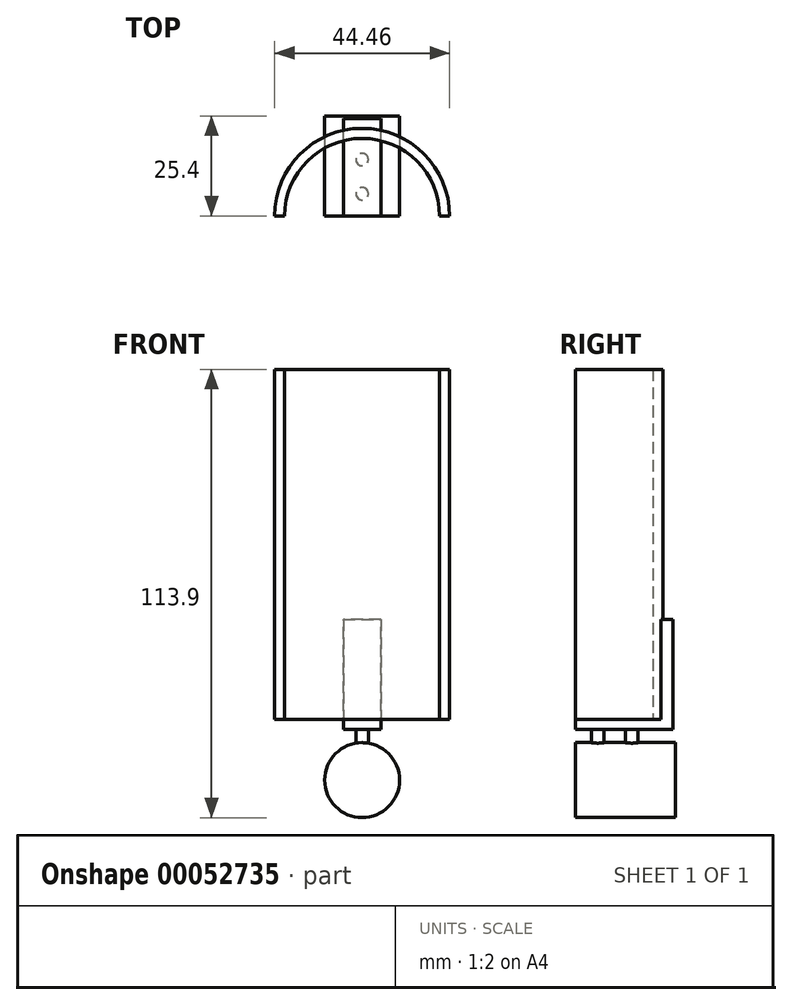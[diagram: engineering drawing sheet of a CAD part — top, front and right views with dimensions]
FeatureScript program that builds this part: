
annotation { "Feature Type Name" : "Feature", "Feature Type Description" : "" }
export const myFeature = defineFeature(function(context is Context, id is Id, definition is map)
    precondition{}
    {
        {
            var Q0;
            Q0=qCreatedBy(makeId("Top.planeOp"),FACE);
            var sketch = newSketch(context, id + "F0", { "sketchPlane" : qUnion([Q0])});
            skCircle(sketch, "E0", {"center": v(0, 0) * mm, "radius": 19.69 * mm});
            skCircle(sketch, "E1", {"center": v(0, 0) * mm, "radius": 22.23 * mm});
            skLineSegment(sketch, "E2", {"start": v(0, 0) * mm, "end": v(22.23, 0) * mm});
            skLineSegment(sketch, "E3", {"start": v(0, 0) * mm, "end": v(-22.23, 0) * mm});
            skSolve(sketch);
        }
        {
            var Q0;
            {var subQ0=sQuery(id+"F0.wireOp",EDGE,"E2");var subQ1=sQuery(id+"F0.wireOp",EDGE,"E0");var subQ2=makeQuery(id+"F0.imprint","INTERSECT",VERTEX,{"derivedFrom":[subQ1,subQ0]});Q0=makeQuery(id+"F0.imprint","IMPRINT",FACE,{"disambiguationData":[TD([[makeQuery(id+"F0.imprint","IMPRINT",EDGE,{"disambiguationData":[TD([[subQ2,-1.0]])],"derivedFrom":subQ1}),-1.0]])]});}
            extrude(context, id + "F1", {"entities" : qUnion([Q0]), "depth" : 88.9 * mm});
        }
        {
            var Q0;
            Q0=qCreatedBy(makeId("Top.planeOp"),FACE);
            var sketch = newSketch(context, id + "F2", { "sketchPlane" : qUnion([Q0])});
            skLineSegment(sketch, "E4.rect.bottom", {"start": v(-4.76, 0) * mm, "end": v(4.76, 0) * mm});
            skLineSegment(sketch, "E4.rect.top", {"start": v(-4.76, 24.77) * mm, "end": v(4.76, 24.77) * mm});
            skLineSegment(sketch, "E4.rect.left", {"start": v(-4.76, 0) * mm, "end": v(-4.76, 24.77) * mm});
            skLineSegment(sketch, "E4.rect.right", {"start": v(4.76, 0) * mm, "end": v(4.76, 24.77) * mm});
            skPoint(sketch, "E4.rect.middle", {"position": v(0, 12.38) * mm});
            skLineSegment(sketch, "E5", {"start": v(0, 22.28) * mm, "end": v(4.76, 22.28) * mm});
            skLineSegment(sketch, "E6", {"start": v(0, 22.28) * mm, "end": v(-4.76, 22.28) * mm});
            skSolve(sketch);
        }
        {
            var Q0;
            Q0 = qSketchRegion(id + "F2", true);
            extrude(context, id + "F3", {"entities" : qUnion([Q0]), "operationType" : NewBodyOperationType.ADD, "oppositeDirection" : true, "depth" : 2.54 * mm});
        }
        {
            var Q0;
            {var subQ0=sQuery(id+"F2.wireOp",EDGE,"E4.rect.left");var subQ1=sQuery(id+"F0.wireOp",EDGE,"E1");var subQ2=sQuery(id+"F2.wireOp",EDGE,"E4.rect.top");var subQ3=sQuery(id+"F2.wireOp",EDGE,"E4.rect.right");Q0=makeQuery(id+"F3.boolean.opBoolean","SPLIT",FACE,{"disambiguationData":[TD([makeQuery(id+"F1.opExtrude","SWEPT_FACE",FACE,{"disambiguationData":[OSD([subQ1])]})])],"derivedFrom":makeQuery(id+"F3.opExtrude","CAP_FACE",FACE,{"disambiguationData":[OSD([sQuery(id+"F2.wireOp",EDGE,"E4.rect.bottom"),subQ2,subQ0,subQ3])],"isStart":true})});}
            extrude(context, id + "F4", {"entities" : qUnion([Q0]), "operationType" : NewBodyOperationType.ADD, "depth" : 25.4 * mm});
        }
        {
            var Q0;
            Q0=qCreatedBy(makeId("Front.planeOp"),FACE);
            var sketch = newSketch(context, id + "F5", { "sketchPlane" : qUnion([Q0])});
            skCircle(sketch, "E7", {"center": v(0, -15.47) * mm, "radius": 9.53 * mm});
            skSolve(sketch);
        }
        {
            var Q0;
            Q0 = qSketchRegion(id + "F5", true);
            extrude(context, id + "F6", {"entities" : qUnion([Q0]), "oppositeDirection" : true, "depth" : 25.4 * mm});
        }
        {
            var Q0;
            Q0=qCreatedBy(makeId("Top.planeOp"),FACE);
            var sketch = newSketch(context, id + "F7", { "sketchPlane" : qUnion([Q0])});
            skCircle(sketch, "E8", {"center": v(0, 5.6) * mm, "radius": 1.59 * mm});
            skCircle(sketch, "E9", {"center": v(0, 14.3) * mm, "radius": 1.59 * mm});
            skSolve(sketch);
        }
        {
            var Q0;
            Q0 = qSketchRegion(id + "F7", true);
            extrude(context, id + "F8", {"entities" : qUnion([Q0]), "operationType" : NewBodyOperationType.ADD, "oppositeDirection" : true, "depth" : 19.05 * mm});
        }
    });
